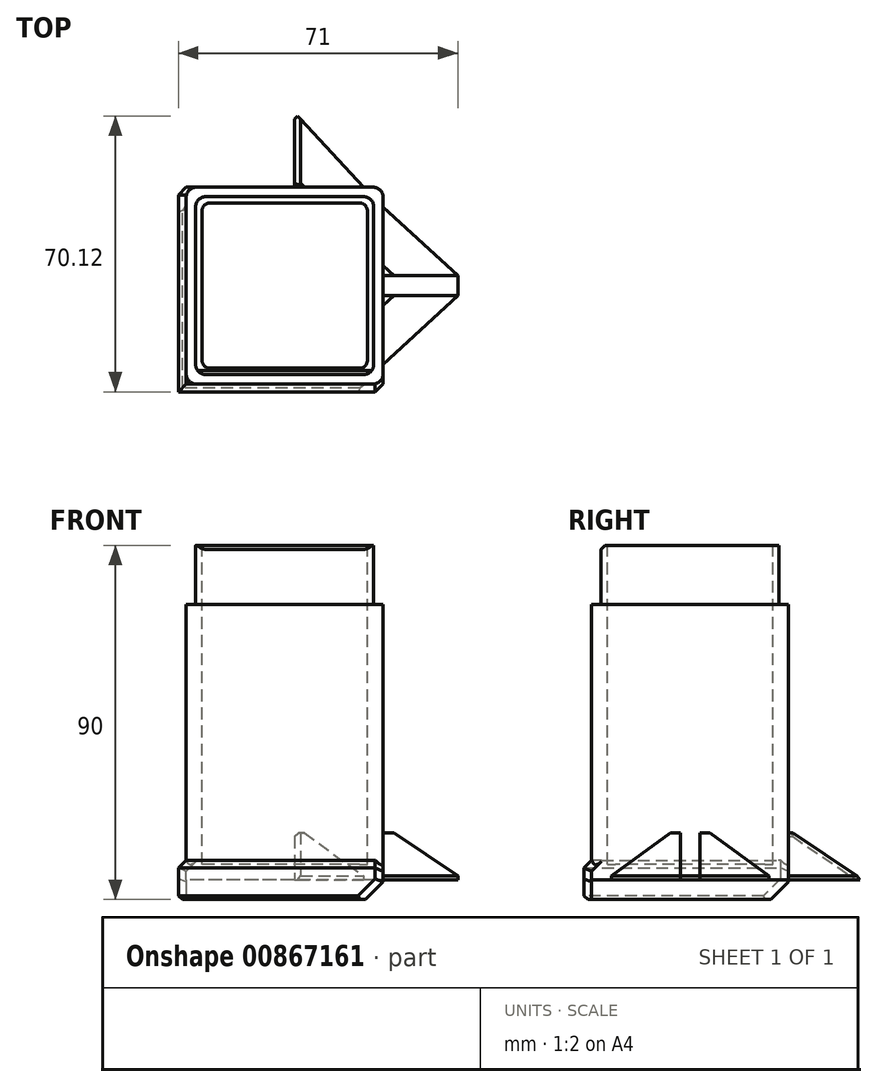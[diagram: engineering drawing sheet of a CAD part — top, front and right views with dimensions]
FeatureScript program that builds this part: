
annotation { "Feature Type Name" : "Feature", "Feature Type Description" : "" }
export const myFeature = defineFeature(function(context is Context, id is Id, definition is map)
    precondition{}
    {
        {
            var Q0;
            Q0=qCreatedBy(makeId("Top.planeOp"),FACE);
            var sketch = newSketch(context, id + "F0", { "sketchPlane" : qUnion([Q0])});
            skLineSegment(sketch, "E0.bottom", {"start": v(25, 25) * mm, "end": v(-25, 25) * mm});
            skLineSegment(sketch, "E0.top", {"start": v(25, -25) * mm, "end": v(-25, -25) * mm});
            skLineSegment(sketch, "E0.left", {"start": v(25, 25) * mm, "end": v(25, -25) * mm});
            skLineSegment(sketch, "E0.right", {"start": v(-25, 25) * mm, "end": v(-25, -25) * mm});
            skPoint(sketch, "E0.middle", {"position": v(0, 0) * mm});
            skSolve(sketch);
        }
        {
            var Q0;
            Q0=qSketchRegion(id+"F0",true);
            extrude(context, id + "F1", {"entities" : qUnion([Q0]), "depth" : 70 * mm, "offsetDistance" : 25 * mm});
        }
        {
            var Q0;
            Q0=makeQuery(id+"F1.opExtrude","CAP_FACE",FACE,{"disambiguationData":[OSD([sQuery(id+"F0.wireOp",EDGE,"E0.bottom"),sQuery(id+"F0.wireOp",EDGE,"E0.top"),sQuery(id+"F0.wireOp",EDGE,"E0.left"),sQuery(id+"F0.wireOp",EDGE,"E0.right")])],"isStart":false});
            var sketch = newSketch(context, id + "F2", { "sketchPlane" : qUnion([Q0])});
            skLineSegment(sketch, "E1.bottom", {"start": v(22.6, 22.6) * mm, "end": v(-22.6, 22.6) * mm});
            skLineSegment(sketch, "E1.top", {"start": v(22.6, -22.6) * mm, "end": v(-22.6, -22.6) * mm});
            skLineSegment(sketch, "E1.left", {"start": v(22.6, 22.6) * mm, "end": v(22.6, -22.6) * mm});
            skLineSegment(sketch, "E1.right", {"start": v(-22.6, 22.6) * mm, "end": v(-22.6, -22.6) * mm});
            skPoint(sketch, "E1.middle", {"position": v(0, 0) * mm});
            skSolve(sketch);
        }
        {
            var Q0;
            Q0=qSketchRegion(id+"F2",true);
            extrude(context, id + "F3", {"entities" : qUnion([Q0]), "operationType" : NewBodyOperationType.ADD, "depth" : 15 * mm, "offsetDistance" : 25 * mm});
        }
        {
            var Q0;
            Q0=makeQuery(id+"F2.imprint","IMPRINT",FACE,{"disambiguationData":[TD([[makeQuery(id+"F2.imprint","IMPRINT",EDGE,{"derivedFrom":sQuery(id+"F2.wireOp",EDGE,"E1.bottom")}),-1.0]])]});
            var sketch = newSketch(context, id + "F4", { "sketchPlane" : qUnion([Q0])});
            skLineSegment(sketch, "E2.bottom", {"start": v(21, 21) * mm, "end": v(-21, 21) * mm});
            skLineSegment(sketch, "E2.top", {"start": v(21, -21) * mm, "end": v(-21, -21) * mm});
            skLineSegment(sketch, "E2.left", {"start": v(21, 21) * mm, "end": v(21, -21) * mm});
            skLineSegment(sketch, "E2.right", {"start": v(-21, 21) * mm, "end": v(-21, -21) * mm});
            skPoint(sketch, "E2.middle", {"position": v(0, 0) * mm});
            skSolve(sketch);
        }
        {
            var Q0;
            Q0=qSketchRegion(id+"F4",true);
            extrude(context, id + "F5", {"entities" : qUnion([Q0]), "operationType" : NewBodyOperationType.REMOVE, "oppositeDirection" : true, "depth" : 66 * mm, "offsetDistance" : 25 * mm, "hasSecondDirection" : true, "secondDirectionBound" : SecondDirectionBoundingType.UP_TO_NEXT, "secondDirectionOppositeDirection" : false, "secondDirectionDepth" : 25 * mm});
        }
        {
            var Q0;
            Q0=makeQuery(id+"F5.boolean.opBoolean","COPY",EDGE,{"derivedFrom":makeQuery(id+"F5.opExtrude","SWEPT_EDGE",EDGE,{"disambiguationData":[OSD([sQuery(id+"F4.wireOp",EDGE,"E2.top"),sQuery(id+"F4.wireOp",EDGE,"E2.right")])]})});
            var Q1;
            Q1=makeQuery(id+"F5.boolean.opBoolean","COPY",EDGE,{"derivedFrom":makeQuery(id+"F5.opExtrude","SWEPT_EDGE",EDGE,{"disambiguationData":[OSD([sQuery(id+"F4.wireOp",EDGE,"E2.bottom"),sQuery(id+"F4.wireOp",EDGE,"E2.right")])]})});
            var Q2;
            Q2=makeQuery(id+"F5.boolean.opBoolean","COPY",EDGE,{"derivedFrom":makeQuery(id+"F5.opExtrude","SWEPT_EDGE",EDGE,{"disambiguationData":[OSD([sQuery(id+"F4.wireOp",EDGE,"E2.bottom"),sQuery(id+"F4.wireOp",EDGE,"E2.left")])]})});
            var Q3;
            Q3=makeQuery(id+"F5.boolean.opBoolean","COPY",EDGE,{"derivedFrom":makeQuery(id+"F5.opExtrude","SWEPT_EDGE",EDGE,{"disambiguationData":[OSD([sQuery(id+"F4.wireOp",EDGE,"E2.top"),sQuery(id+"F4.wireOp",EDGE,"E2.left")])]})});
            fillet(context, id + "F6", {"entities" : qUnion([Q0, Q1, Q2, Q3]), "radius" : 2 * mm, "tangentPropagation" : true, "allowEdgeOverflow" : false});
        }
        {
            var Q0;
            Q0=makeQuery(id+"F3.opExtrude","CAP_EDGE",EDGE,{"disambiguationData":[OSD([sQuery(id+"F2.wireOp",EDGE,"E1.top")])],"isStart":false});
            chamfer(context, id + "F7", {"entities" : qUnion([Q0]), "width" : 1 * mm, "tangentPropagation" : true});
        }
        {
            var Q0;
            Q0=qCreatedBy(makeId("Top.planeOp"),FACE);
            cPlane(context, id + "F8", {"entities" : qUnion([Q0]), "cplaneType" : CPlaneType.OFFSET, "offset" : 1 * mm, "width" : 150 * mm, "height" : 150 * mm});
        }
        {
            var Q0;
            Q0=qCreatedBy(makeId("Top.planeOp"),FACE);
            var sketch = newSketch(context, id + "F9", { "sketchPlane" : qUnion([Q0])});
            skLineSegment(sketch, "E3", {"start": v(25, 20) * mm, "end": v(25, -20) * mm});
            skPoint(sketch, "E4", {"position": v(25, 0) * mm});
            skLineSegment(sketch, "E5", {"start": v(44, 2.5) * mm, "end": v(25, 20) * mm});
            skLineSegment(sketch, "E6", {"start": v(44, -2.5) * mm, "end": v(25, -20) * mm});
            skPoint(sketch, "E7", {"position": v(44, 2.5) * mm});
            skPoint(sketch, "E8", {"position": v(44, -2.5) * mm});
            skLineSegment(sketch, "E9", {"start": v(44, 2.5) * mm, "end": v(44, -2.5) * mm});
            skSolve(sketch);
        }
        {
            var Q0;
            Q0=qSketchRegion(id+"F9",true);
            extrude(context, id + "F10", {"entities" : qUnion([Q0]), "operationType" : NewBodyOperationType.ADD, "depth" : 12 * mm, "offsetDistance" : 25 * mm});
        }
        {
            var Q0;
            Q0=makeQuery(id+"F10.opExtrude","CAP_EDGE",EDGE,{"disambiguationData":[OSD([sQuery(id+"F9.wireOp",EDGE,"E5")])],"isStart":false});
            var Q1;
            Q1=makeQuery(id+"F10.opExtrude","CAP_EDGE",EDGE,{"disambiguationData":[OSD([sQuery(id+"F9.wireOp",EDGE,"E6")])],"isStart":false});
            chamfer(context, id + "F11", {"entities" : qUnion([Q0, Q1]), "width" : 11 * mm, "tangentPropagation" : true});
        }
        {
            var Q0;
            Q0=qCreatedBy(id+"F8.planeOp",FACE);
            var sketch = newSketch(context, id + "F12", { "sketchPlane" : qUnion([Q0])});
            skLineSegment(sketch, "E10.bottom", {"start": v(25, 2.5) * mm, "end": v(45, 2.5) * mm});
            skLineSegment(sketch, "E10.top", {"start": v(25, -2.5) * mm, "end": v(45, -2.5) * mm});
            skLineSegment(sketch, "E10.left", {"start": v(25, 2.5) * mm, "end": v(25, -2.5) * mm});
            skLineSegment(sketch, "E10.right", {"start": v(45, 2.5) * mm, "end": v(45, -2.5) * mm});
            skPoint(sketch, "E11", {"position": v(25, 0) * mm});
            skSolve(sketch);
        }
        {
            var Q0;
            Q0=qSketchRegion(id+"F12",true);
            extrude(context, id + "F13", {"entities" : qUnion([Q0]), "operationType" : NewBodyOperationType.REMOVE, "depth" : 20 * mm, "offsetDistance" : 25 * mm});
        }
        {
            var Q0;
            Q0=qCreatedBy(makeId("Top.planeOp"),FACE);
            var sketch = newSketch(context, id + "F14", { "sketchPlane" : qUnion([Q0])});
            skLineSegment(sketch, "E12", {"start": v(2.5, 44) * mm, "end": v(20, 25) * mm});
            skLineSegment(sketch, "E13", {"start": v(-2.5, 44) * mm, "end": v(2.5, 44) * mm});
            skPoint(sketch, "E14", {"position": v(0, 44) * mm});
            skLineSegment(sketch, "E15", {"start": v(-2.5, 44) * mm, "end": v(-2.5, 25) * mm});
            skLineSegment(sketch, "E16", {"start": v(-2.5, 25) * mm, "end": v(20, 25) * mm});
            skSolve(sketch);
        }
        {
            var Q0;
            Q0=qSketchRegion(id+"F14",true);
            extrude(context, id + "F15", {"entities" : qUnion([Q0]), "operationType" : NewBodyOperationType.ADD, "depth" : 12 * mm, "offsetDistance" : 25 * mm});
        }
        {
            var Q0;
            Q0=makeQuery(id+"F15.opExtrude","CAP_EDGE",EDGE,{"disambiguationData":[OSD([sQuery(id+"F14.wireOp",EDGE,"c6486ea1-f339-4a03-8ac4-994e5f46793e")])],"isStart":false});
            var Q1;
            Q1=makeQuery(id+"F15.opExtrude","CAP_EDGE",EDGE,{"disambiguationData":[OSD([sQuery(id+"F14.wireOp",EDGE,"E12")])],"isStart":false});
            chamfer(context, id + "F16", {"entities" : qUnion([Q0, Q1]), "width" : 11 * mm, "tangentPropagation" : true});
        }
        {
            var Q0;
            Q0=qCreatedBy(makeId("Top.planeOp"),FACE);
            var sketch = newSketch(context, id + "F17", { "sketchPlane" : qUnion([Q0])});
            skLineSegment(sketch, "E17.bottom", {"start": v(-2.5, 25) * mm, "end": v(-2.5, 45) * mm});
            skLineSegment(sketch, "E17.top", {"start": v(2.5, 25) * mm, "end": v(2.5, 45) * mm});
            skLineSegment(sketch, "E17.left", {"start": v(-2.5, 25) * mm, "end": v(2.5, 25) * mm});
            skLineSegment(sketch, "E17.right", {"start": v(-2.5, 45) * mm, "end": v(2.5, 45) * mm});
            skPoint(sketch, "E18", {"position": v(0, 25) * mm});
            skSolve(sketch);
        }
        {
            var Q0;
            Q0=qSketchRegion(id+"F17",true);
            extrude(context, id + "F18", {"entities" : qUnion([Q0]), "operationType" : NewBodyOperationType.REMOVE, "depth" : 20 * mm, "offsetDistance" : 25 * mm});
        }
        {
            var Q0;
            Q0=makeQuery(id+"F18.boolean.opBoolean","INTERSECT",EDGE,{"derivedFrom":[makeQuery(id+"F16.opChamfer","BLEND_FACE",FACE,{"disambiguationData":[OSD([sQuery(id+"F14.wireOp",EDGE,"E12")])]}),makeQuery(id+"F18.opExtrude","SWEPT_FACE",FACE,{"disambiguationData":[OSD([sQuery(id+"F17.wireOp",EDGE,"E17.top")])]})]});
            var Q1;
            Q1=makeQuery(id+"F18.boolean.opBoolean","INTERSECT",EDGE,{"derivedFrom":[makeQuery(id+"F15.opExtrude","CAP_FACE",FACE,{"disambiguationData":[OSD([sQuery(id+"F14.wireOp",EDGE,"E12"),sQuery(id+"F14.wireOp",EDGE,"E13"),sQuery(id+"F14.wireOp",EDGE,"E15"),sQuery(id+"F14.wireOp",EDGE,"E16")])],"isStart":false}),makeQuery(id+"F18.opExtrude","SWEPT_FACE",FACE,{"disambiguationData":[OSD([sQuery(id+"F17.wireOp",EDGE,"E17.top")])]})]});
            chamfer(context, id + "F19", {"entities" : qUnion([Q0, Q1]), "width" : 1 * mm, "tangentPropagation" : true});
        }
        {
            var Q0;
            Q0=qCreatedBy(makeId("Top.planeOp"),FACE);
            var sketch = newSketch(context, id + "F20", { "sketchPlane" : qUnion([Q0])});
            skLineSegment(sketch, "E19", {"start": v(-27, 25) * mm, "end": v(-27, -27) * mm});
            skLineSegment(sketch, "E20", {"start": v(-27, -27) * mm, "end": v(25, -27) * mm});
            skLineSegment(sketch, "E21", {"start": v(25, -27) * mm, "end": v(25, -25) * mm});
            skLineSegment(sketch, "E22", {"start": v(25, -25) * mm, "end": v(-25, -25) * mm});
            skLineSegment(sketch, "E23", {"start": v(-25, -25) * mm, "end": v(-25, 25) * mm});
            skLineSegment(sketch, "E24", {"start": v(-25, 25) * mm, "end": v(-27, 25) * mm});
            skSolve(sketch);
        }
        {
            var Q0;
            Q0 = qSketchRegion(id + "F20", true);
            extrude(context, id + "F21", {"entities" : qUnion([Q0]), "operationType" : NewBodyOperationType.ADD, "endBound" : BoundingType.SYMMETRIC, "depth" : 10 * mm, "offsetDistance" : 25 * mm});
        }
        {
            var Q0;
            Q0=makeQuery(id+"F1.opExtrude","SWEPT_EDGE",EDGE,{"disambiguationData":[OSD([sQuery(id+"F0.wireOp",EDGE,"E0.bottom"),sQuery(id+"F0.wireOp",EDGE,"E0.left")])]});
            var Q1;
            Q1=makeQuery(id+"F3.opExtrude","SWEPT_EDGE",EDGE,{"disambiguationData":[OSD([sQuery(id+"F2.wireOp",EDGE,"E1.bottom"),sQuery(id+"F2.wireOp",EDGE,"E1.right")])]});
            var Q2;
            Q2=makeQuery(id+"F1.opExtrude","SWEPT_EDGE",EDGE,{"disambiguationData":[OSD([sQuery(id+"F0.wireOp",EDGE,"E0.bottom"),sQuery(id+"F0.wireOp",EDGE,"E0.right")])]});
            var Q3;
            Q3=makeQuery(id+"F3.opExtrude","SWEPT_EDGE",EDGE,{"disambiguationData":[OSD([sQuery(id+"F2.wireOp",EDGE,"E1.bottom"),sQuery(id+"F2.wireOp",EDGE,"E1.left")])]});
            var Q4;
            Q4=makeQuery(id+"F3.opExtrude","SWEPT_EDGE",EDGE,{"disambiguationData":[OSD([sQuery(id+"F2.wireOp",EDGE,"E1.top"),sQuery(id+"F2.wireOp",EDGE,"E1.left")])]});
            var Q5;
            Q5=makeQuery(id+"F1.opExtrude","SWEPT_EDGE",EDGE,{"disambiguationData":[OSD([sQuery(id+"F0.wireOp",EDGE,"E0.top"),sQuery(id+"F0.wireOp",EDGE,"E0.left")])]});
            var Q6;
            Q6=makeQuery(id+"F3.opExtrude","SWEPT_EDGE",EDGE,{"disambiguationData":[OSD([sQuery(id+"F2.wireOp",EDGE,"E1.top"),sQuery(id+"F2.wireOp",EDGE,"E1.right")])]});
            var Q7;
            Q7=makeQuery(id+"F1.opExtrude","SWEPT_EDGE",EDGE,{"disambiguationData":[OSD([sQuery(id+"F0.wireOp",EDGE,"E0.top"),sQuery(id+"F0.wireOp",EDGE,"E0.right")])]});
            fillet(context, id + "F22", {"entities" : qUnion([Q0, Q1, Q2, Q3, Q4, Q5, Q6, Q7]), "radius" : 2.5 * mm, "tangentPropagation" : true, "allowEdgeOverflow" : false});
        }
        {
            var Q0;
            Q0=makeQuery(id+"F21.opExtrude","CAP_EDGE",EDGE,{"disambiguationData":[OSD([sQuery(id+"F20.wireOp",EDGE,"E19")])],"isStart":false});
            var Q1;
            Q1=makeQuery(id+"F21.opExtrude","CAP_EDGE",EDGE,{"disambiguationData":[OSD([sQuery(id+"F20.wireOp",EDGE,"E20")])],"isStart":false});
            chamfer(context, id + "F23", {"entities" : qUnion([Q0, Q1]), "width" : 2 * mm, "tangentPropagation" : true});
        }
        {
            var Q0;
            Q0=makeQuery(id+"F21.opExtrude","CAP_EDGE",EDGE,{"disambiguationData":[OSD([sQuery(id+"F20.wireOp",EDGE,"E24")])],"isStart":true});
            var Q1;
            Q1=makeQuery(id+"F21.opExtrude","CAP_EDGE",EDGE,{"disambiguationData":[OSD([sQuery(id+"F20.wireOp",EDGE,"E21")])],"isStart":true});
            chamfer(context, id + "F24", {"entities" : qUnion([Q0, Q1]), "width" : 4.5 * mm, "tangentPropagation" : true});
        }
        {
            var Q0;
            Q0=makeQuery(id+"F23.opChamfer","BLEND_EDGE",EDGE,{"blendedFrom":[makeQuery(id+"F21.opExtrude","CAP_EDGE",EDGE,{"disambiguationData":[OSD([sQuery(id+"F20.wireOp",EDGE,"E19")])],"isStart":false}),makeQuery(id+"F21.opExtrude","SWEPT_FACE",FACE,{"disambiguationData":[OSD([sQuery(id+"F20.wireOp",EDGE,"E24")])]})],"blendedInto":[makeQuery(id+"F21.opExtrude","SWEPT_FACE",FACE,{"disambiguationData":[OSD([sQuery(id+"F20.wireOp",EDGE,"E24")])]})]});
            var Q1;
            Q1=makeQuery(id+"F21.opExtrude","SWEPT_EDGE",EDGE,{"disambiguationData":[OSD([sQuery(id+"F20.wireOp",EDGE,"E19"),sQuery(id+"F20.wireOp",EDGE,"E24")])]});
            var Q2;
            Q2=makeQuery(id+"F24.opChamfer","BLEND_EDGE",EDGE,{"blendedFrom":[makeQuery(id+"F21.opExtrude","CAP_EDGE",EDGE,{"disambiguationData":[OSD([sQuery(id+"F20.wireOp",EDGE,"E24")])],"isStart":true}),makeQuery(id+"F21.opExtrude","SWEPT_FACE",FACE,{"disambiguationData":[OSD([sQuery(id+"F20.wireOp",EDGE,"E19")])]})],"blendedInto":[makeQuery(id+"F21.opExtrude","SWEPT_FACE",FACE,{"disambiguationData":[OSD([sQuery(id+"F20.wireOp",EDGE,"E19")])]})]});
            var Q3;
            Q3=makeQuery(id+"F24.opChamfer","BLEND_EDGE",EDGE,{"blendedFrom":[makeQuery(id+"F21.opExtrude","CAP_EDGE",EDGE,{"disambiguationData":[OSD([sQuery(id+"F20.wireOp",EDGE,"E21")])],"isStart":true}),makeQuery(id+"F21.opExtrude","SWEPT_FACE",FACE,{"disambiguationData":[OSD([sQuery(id+"F20.wireOp",EDGE,"E20")])]})],"blendedInto":[makeQuery(id+"F21.opExtrude","SWEPT_FACE",FACE,{"disambiguationData":[OSD([sQuery(id+"F20.wireOp",EDGE,"E20")])]})]});
            var Q4;
            Q4=makeQuery(id+"F21.opExtrude","SWEPT_EDGE",EDGE,{"disambiguationData":[OSD([sQuery(id+"F20.wireOp",EDGE,"E20"),sQuery(id+"F20.wireOp",EDGE,"E21")])]});
            var Q5;
            Q5=makeQuery(id+"F23.opChamfer","BLEND_EDGE",EDGE,{"blendedFrom":[makeQuery(id+"F21.opExtrude","CAP_EDGE",EDGE,{"disambiguationData":[OSD([sQuery(id+"F20.wireOp",EDGE,"E20")])],"isStart":false}),makeQuery(id+"F21.opExtrude","SWEPT_FACE",FACE,{"disambiguationData":[OSD([sQuery(id+"F20.wireOp",EDGE,"E21")])]})],"blendedInto":[makeQuery(id+"F21.opExtrude","SWEPT_FACE",FACE,{"disambiguationData":[OSD([sQuery(id+"F20.wireOp",EDGE,"E21")])]})]});
            chamfer(context, id + "F25", {"entities" : qUnion([Q0, Q1, Q2, Q3, Q4, Q5]), "width" : 2 * mm, "tangentPropagation" : true});
        }
        {
            var Q0;
            Q0=makeQuery(id+"F21.opExtrude","CAP_EDGE",EDGE,{"disambiguationData":[OSD([sQuery(id+"F20.wireOp",EDGE,"E19")])],"isStart":true});
            var Q1;
            Q1=makeQuery(id+"F21.opExtrude","CAP_EDGE",EDGE,{"disambiguationData":[OSD([sQuery(id+"F20.wireOp",EDGE,"E20")])],"isStart":true});
            chamfer(context, id + "F26", {"entities" : qUnion([Q0, Q1]), "width" : 1 * mm, "tangentPropagation" : true});
        }
    });
